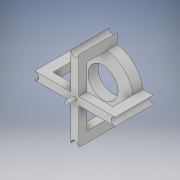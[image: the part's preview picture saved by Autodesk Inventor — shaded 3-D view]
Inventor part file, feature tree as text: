
AUTODESK INVENTOR PART (.ipt)
format: ipt  version: 2019 (Build 230136000, 136)  size: 204,800 bytes
history: native  units: mm
features: extrude x5, sketch x5, plane x1
ambient origin geometry x8: Origin, YZ Plane, XZ Plane, XY Plane, X Axis, Y Axis, Z Axis, Center Point
bodies: Solid1 (feature_tree)
feature tree (11):
  extrude  "Extrusion1"  Depth=4.0mm
  extrude  "Extrusion2"  Depth=4.0mm
  sketch  "Sketch3"  dims[d4=30.0mm d5=15.0mm]
  plane  "Work Plane1"
  sketch  "Sketch4"  dims[d6=5.0mm d7=0.0mm d8=17.0mm]
  extrude  "Extrusion4"  Depth=15.0mm
  extrude  "Extrusion5"  Depth=5.0mm
  extrude  "Extrusion6"  Depth=1.0mm TaperAngle=0.0deg
  sketch  "Sketch1"  dims[d0=4.0mm d1=4.0mm]
  sketch  "Sketch2"  dims[d2=4.0mm d3=4.0mm]
  sketch  "Sketch5"  dims[d9=28.0mm d10=1.0mm d11=0.0mm d14=14.0mm d15=0.0mm d16=4.0mm d17=0.0mm d18=2.0mm d19=4.0mm d20=0.0mm]
